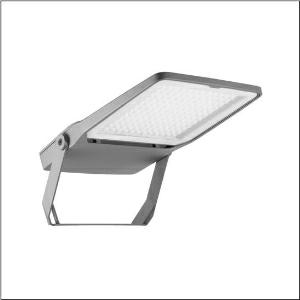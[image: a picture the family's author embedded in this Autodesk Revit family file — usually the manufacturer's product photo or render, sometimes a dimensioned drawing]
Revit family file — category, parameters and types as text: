
# Revit family: floodlight_fl_20_midi___pl52_5xa7682d2d1ac_9f95
name_source: partatom
category: Lighting Fixtures
units: mm (PartAtom-declared; Revit-internal decimal feet)

## family parameters
Cut with Voids When Loaded = No
Host = Face
Light Source = No
Part Type = Normal
Room Calculation Point = No
Round Connector Dimension = Use Diameter
Shared = No

## types (1)
- --- (1 x LED 4000K / CRI = 70 (unbekannt), 17990 lm, 4000K)
    Apparent Load = 142 VA
    CIE Flux Codes = 27 59 98 100 100
    Color Rendering = 70
    Color Temperature = 4000K
    Default Elevation = 1800 mm
    Description = Floodlight FL 20 midi, floodlight, primary light control with lens, of plastic, primary optical cover: protective disc, of toughened safety glass, transparent, light distribution: PL52, light emission: direct distribution, primary light characteristic: asymmetric, installation type: surface-mounted, LED, High Power LED, rated luminous flux: 17.990lm, luminous efficacy: 127lm/W, light colour: 740, colour temperature: 4000K, control gear: ECG Plus, control: flexible luminous flux parameterisation, time-dependent luminous flux control, digital communication interface, power reduction, overheat protection, electronic power reduction, with terminal, 5-pole, max. 2.5mm², mains connection: 220..240V, AC, 50/60Hz, rated input power: 142W, LED unit, of diecast aluminium, powder-coated, Siteco® metallic grey (DB 702S), corrosivity category C5 mid according to DIN EN ISO 12944, incl. 1x M20 cable gland for cable Ø 6.5..12mm, length: 654mm, width: 450mm, height: 76mm, housing frame, of diecast aluminium, powder-coated, Siteco® metallic grey (DB 702S), mounting bracket, of steel, powder-coated, Siteco® metallic grey (DB 702S), DALI, protection rating (complete): IP66, insulation class (complete): insulation class II (safety insulation), certification: CE, ENEC, VDE, protection symbol: D, permissible operating ambient temperature: -40..+40°C, permissible operating ambient temperature for outdoor applications: -40..+50°C, standard: DIN EN 12944, packaging unit: 1 piece

Light Distribution: PL52
    Height = 76 mm
    Lamp = 1 x LED 4000K / CRI >= 70 (unbekannt)
    Lamp Light Flux = 17990 lm
    Lamp count = 1
    Length = 672 mm
    Luminous efficacy = 127 lm/W
    Manufacturer = Siteco
    ModVariant = No
    Model = 5XA7682D2D1AC
    Mounting Place = Wall
    Mounting Type = Surface mounted
    Number of Poles = 1
    OnlyDefault = Yes
    Power Factor = 1
    Product Name = Floodlight FL 20 midi | PL52
    Product group = floodlight | wall mounted
    ProductGroupID = 2001
    Protection Class = Protection class II
    Protection Degree = IP 66
    RLX_Detail_Level = 1
    RLX_Emergency_Light_Flux = 0 lm
    RLX_Emergency_Type = 0
    RLX_Emergency_Type_DB = No
    RlxData = <blob elided: 97813 chars, md5=2e722c79>
    Socket = socket
    Standby Power = 0 W
    System Light Flux = 17990 lm
    System Power = 142 W
    Type Comments = factory setting: luminous flux: 100 % | dim-lin: 254 | 489 mA
    Type Image = l_1005943.jpg
    URL = http://relux.com
    VarID = @adj_147931
    Voltage = 0 V
    Weight = 0.00 kg
    Width = 450 mm

## geometry (parser evidence)
native form markers: Blend x4, Sweep x12
no freeform markers — native parametric forms only
